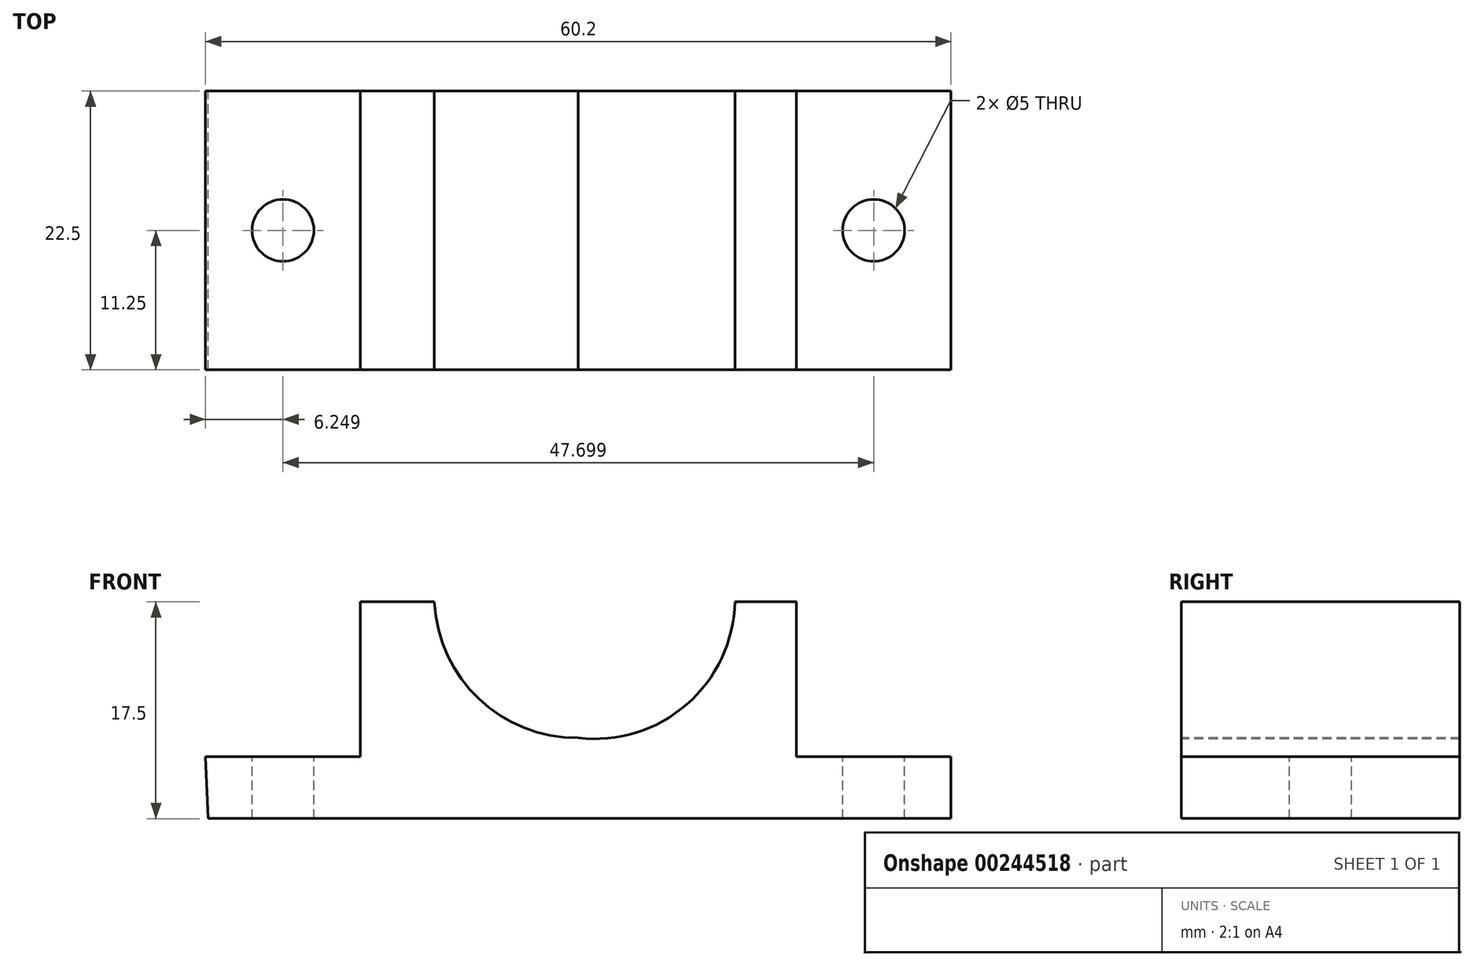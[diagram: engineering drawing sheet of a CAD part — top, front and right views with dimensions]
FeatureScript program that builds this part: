
annotation { "Feature Type Name" : "Feature", "Feature Type Description" : "" }
export const myFeature = defineFeature(function(context is Context, id is Id, definition is map)
    precondition{}
    {
        {
            var Q0;
            Q0=qCreatedBy(makeId("Front.planeOp"),FACE);
            var sketch = newSketch(context, id + "F0", { "sketchPlane" : qUnion([Q0])});
            skLineSegment(sketch, "E0", {"start": v(-18.27, -20.36) * mm, "end": v(41.73, -20.37) * mm});
            skLineSegment(sketch, "E1", {"start": v(41.73, -20.37) * mm, "end": v(41.73, -15.37) * mm});
            skLineSegment(sketch, "E2", {"start": v(41.73, -15.37) * mm, "end": v(29.23, -15.37) * mm});
            skLineSegment(sketch, "E3", {"start": v(29.23, -15.37) * mm, "end": v(29.23, -2.87) * mm});
            skLineSegment(sketch, "E4", {"start": v(29.23, -2.87) * mm, "end": v(-5.97, -2.87) * mm});
            skLineSegment(sketch, "E5", {"start": v(-5.97, -2.87) * mm, "end": v(-5.97, -15.37) * mm});
            skLineSegment(sketch, "E6", {"start": v(-5.97, -15.37) * mm, "end": v(-18.47, -15.37) * mm});
            skLineSegment(sketch, "E7", {"start": v(-18.27, -20.36) * mm, "end": v(-18.47, -15.37) * mm});
            skSolve(sketch);
        }
        {
            var Q0;
            Q0=makeQuery(id+"F0.imprint","IMPRINT",FACE,{"disambiguationData":[TD([[makeQuery(id+"F0.imprint","IMPRINT",EDGE,{"derivedFrom":sQuery(id+"F0.wireOp",EDGE,"E0")}),1.0]])]});
            extrude(context, id + "F1", {"entities" : qUnion([Q0]), "depth" : 22.5 * mm});
        }
        {
            var Q0;
            Q0=makeQuery(id+"F1.opExtrude","SWEPT_FACE",FACE,{"disambiguationData":[OSD([sQuery(id+"F0.wireOp",EDGE,"E2")])]});
            var sketch = newSketch(context, id + "F2", { "sketchPlane" : qUnion([Q0])});
            skCircle(sketch, "E8", {"center": v(35.48, -11.25) * mm, "radius": 2.5 * mm});
            skSolve(sketch);
        }
        {
            var Q0;
            Q0 = qSketchRegion(id + "F2", true);
            extrude(context, id + "F3", {"entities" : qUnion([Q0]), "operationType" : NewBodyOperationType.REMOVE, "endBound" : BoundingType.THROUGH_ALL, "oppositeDirection" : true, "depth" : 17.3 * mm});
        }
        {
            var Q0;
            Q0=makeQuery(id+"F1.opExtrude","SWEPT_FACE",FACE,{"disambiguationData":[OSD([sQuery(id+"F0.wireOp",EDGE,"E6")])]});
            var sketch = newSketch(context, id + "F4", { "sketchPlane" : qUnion([Q0])});
            skCircle(sketch, "E9", {"center": v(-12.22, -11.25) * mm, "radius": 2.5 * mm});
            skSolve(sketch);
        }
        {
            var Q0;
            Q0 = qSketchRegion(id + "F4", true);
            extrude(context, id + "F5", {"entities" : qUnion([Q0]), "operationType" : NewBodyOperationType.REMOVE, "endBound" : BoundingType.THROUGH_ALL, "oppositeDirection" : true, "depth" : 25 * mm});
        }
        {
            var Q0;
            Q0=makeQuery(id+"F1.opExtrude","CAP_FACE",FACE,{"disambiguationData":[OSD([sQuery(id+"F0.wireOp",EDGE,"E0"),sQuery(id+"F0.wireOp",EDGE,"E1"),sQuery(id+"F0.wireOp",EDGE,"E2"),sQuery(id+"F0.wireOp",EDGE,"E3"),sQuery(id+"F0.wireOp",EDGE,"E4"),sQuery(id+"F0.wireOp",EDGE,"E5"),sQuery(id+"F0.wireOp",EDGE,"E6"),sQuery(id+"F0.wireOp",EDGE,"E7")])],"isStart":false});
            var sketch = newSketch(context, id + "F6", { "sketchPlane" : qUnion([Q0])});
            skArc(sketch, "E10", {"start": v(11.63, -13.86) * mm, "mid": v(20.38, -11.15) * mm, "end": v(24.28, -2.87) * mm});
            skArc(sketch, "E11", {"start": v(0, -2.87) * mm, "mid": v(3.6, -10.7) * mm, "end": v(11.63, -13.86) * mm});
            skLineSegment(sketch, "E12", {"start": v(0, -2.87) * mm, "end": v(11.63, -2.87) * mm});
            skLineSegment(sketch, "E13", {"start": v(24.28, -2.87) * mm, "end": v(11.63, -2.87) * mm});
            skSolve(sketch);
        }
        {
            var Q0;
            Q0=makeQuery(id+"F6.imprint","IMPRINT",FACE,{"disambiguationData":[TD([[makeQuery(id+"F6.imprint","IMPRINT",EDGE,{"derivedFrom":sQuery(id+"F6.wireOp",EDGE,"E10")}),1.0]])]});
            extrude(context, id + "F7", {"entities" : qUnion([Q0]), "operationType" : NewBodyOperationType.REMOVE, "endBound" : BoundingType.THROUGH_ALL, "oppositeDirection" : true, "depth" : 25 * mm});
        }
    });
